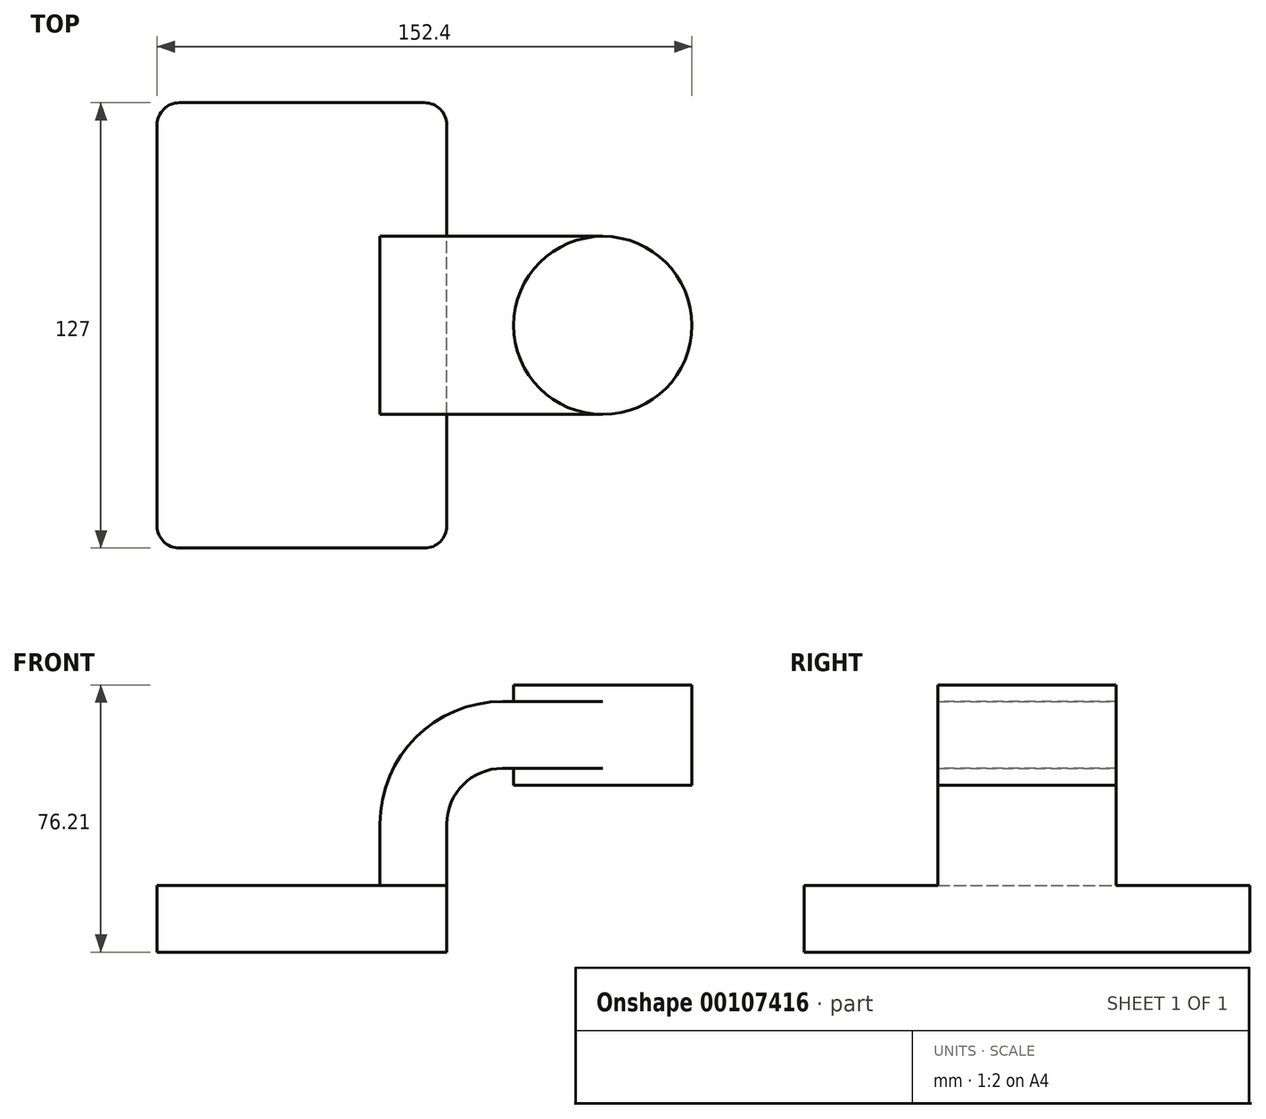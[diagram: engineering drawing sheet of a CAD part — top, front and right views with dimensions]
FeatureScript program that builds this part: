
annotation { "Feature Type Name" : "Feature", "Feature Type Description" : "" }
export const myFeature = defineFeature(function(context is Context, id is Id, definition is map)
    precondition{}
    {
        {
            var Q0;
            Q0=qCreatedBy(makeId("Front.planeOp"),FACE);
            var sketch = newSketch(context, id + "F0", { "sketchPlane" : qUnion([Q0])});
            skLineSegment(sketch, "E0.bottom", {"start": v(41.27, 9.53) * mm, "end": v(-41.28, 9.53) * mm});
            skLineSegment(sketch, "E0.top", {"start": v(41.28, -9.52) * mm, "end": v(-41.27, -9.52) * mm});
            skLineSegment(sketch, "E0.left", {"start": v(41.28, 9.53) * mm, "end": v(41.28, -9.52) * mm});
            skLineSegment(sketch, "E0.right", {"start": v(-41.28, 9.53) * mm, "end": v(-41.27, -9.52) * mm});
            skPoint(sketch, "E0.middle", {"position": v(0, 0) * mm});
            skLineSegment(sketch, "E1.bottom", {"start": v(60.33, 38.1) * mm, "end": v(111.13, 38.1) * mm});
            skLineSegment(sketch, "E1.top", {"start": v(60.33, 66.68) * mm, "end": v(111.13, 66.68) * mm});
            skLineSegment(sketch, "E1.left", {"start": v(60.33, 38.1) * mm, "end": v(60.33, 66.67) * mm});
            skLineSegment(sketch, "E1.right", {"start": v(111.13, 38.1) * mm, "end": v(111.13, 66.68) * mm});
            skPoint(sketch, "E1.middle", {"position": v(85.73, 52.39) * mm});
            skLineSegment(sketch, "E2", {"start": v(41.27, 9.53) * mm, "end": v(41.27, 27) * mm});
            skArc(sketch, "E3", {"start": v(41.27, 27) * mm, "mid": v(45.92, 38.23) * mm, "end": v(57.15, 42.88) * mm});
            skLineSegment(sketch, "E4", {"start": v(57.15, 42.88) * mm, "end": v(85.73, 42.88) * mm});
            skLineSegment(sketch, "E5.0", {"start": v(57.15, 61.93) * mm, "end": v(85.73, 61.93) * mm});
            skArc(sketch, "E5.1", {"start": v(22.23, 27) * mm, "mid": v(32.45, 51.7) * mm, "end": v(57.15, 61.93) * mm});
            skLineSegment(sketch, "E5.2", {"start": v(22.22, 9.53) * mm, "end": v(22.22, 27) * mm});
            skLineSegment(sketch, "E6", {"start": v(85.73, 66.68) * mm, "end": v(85.73, 38.1) * mm});
            skFitSpline(sketch, "E7", {"points": [v(-41.28, 9.52) * mm, v(57.15, 61.93) * mm], "startDerivative": vector(0.32, 75.35) * mm, "endDerivative": vector(119.06, -1.1) * mm});
            skSolve(sketch);
        }
        {
            var Q0;
            Q0=makeQuery(id+"F0.imprint","IMPRINT",FACE,{"disambiguationData":[TD([[makeQuery(id+"F0.imprint","IMPRINT",EDGE,{"derivedFrom":sQuery(id+"F0.wireOp",EDGE,"E0.top")}),-1.0]])]});
            extrude(context, id + "F1", {"entities" : qUnion([Q0]), "endBound" : BoundingType.SYMMETRIC, "depth" : 127 * mm});
        }
        {
            var Q0;
            {var subQ1=sQuery(id+"F0.wireOp",EDGE,"E2");Q0=makeQuery(id+"F0.imprint","IMPRINT",FACE,{"disambiguationData":[TD([[makeQuery(id+"F0.imprint","IMPRINT",EDGE,{"derivedFrom":subQ1}),1.0]])]});}
            extrude(context, id + "F2", {"entities" : qUnion([Q0]), "operationType" : NewBodyOperationType.ADD, "endBound" : BoundingType.SYMMETRIC, "depth" : 50.8 * mm});
        }
        {
            var Q0;
            Q0=makeQuery(id+"F0.imprint","IMPRINT",FACE,{"disambiguationData":[TD([[makeQuery(id+"F0.imprint","IMPRINT",EDGE,{"derivedFrom":sQuery(id+"F0.wireOp",EDGE,"E5.1")}),1.0]])]});
            extrude(context, id + "F3", {"entities" : qUnion([Q0]), "operationType" : NewBodyOperationType.ADD, "endBound" : BoundingType.SYMMETRIC, "depth" : 15.88 * mm});
        }
        {
            var Q0;
            {var subQ0=sQuery(id+"F0.wireOp",EDGE,"E4");var subQ1=sQuery(id+"F0.wireOp",EDGE,"E1.left");var subQ2=makeQuery(id+"F0.imprint","INTERSECT",VERTEX,{"derivedFrom":[subQ1,subQ0]});Q0=makeQuery(id+"F0.imprint","IMPRINT",FACE,{"disambiguationData":[TD([[makeQuery(id+"F0.imprint","IMPRINT",EDGE,{"disambiguationData":[TD([[subQ2,-1.0]])],"derivedFrom":subQ1}),-1.0]])]});}
            extrude(context, id + "F4", {"entities" : qUnion([Q0]), "operationType" : NewBodyOperationType.ADD, "endBound" : BoundingType.SYMMETRIC, "depth" : 50.8 * mm});
        }
        {
            var Q0;
            {var subQ0=sQuery(id+"F0.wireOp",EDGE,"E1.right");Q0=makeQuery(id+"F0.imprint","IMPRINT",FACE,{"disambiguationData":[TD([[makeQuery(id+"F0.imprint","IMPRINT",EDGE,{"derivedFrom":subQ0}),1.0]])]});}
            var Q1;
            Q1=sQuery(id+"F0.wireOp",EDGE,"E6");
            revolve(context, id + "F5", {"operationType" : NewBodyOperationType.ADD, "entities" : qUnion([Q0]), "axis" : qUnion([Q1]), "revolveType" : RevolveType.FULL});
        }
        {
            var Q0;
            Q0=makeQuery(id+"F1.opExtrude","CAP_EDGE",EDGE,{"disambiguationData":[OSD([sQuery(id+"F0.wireOp",EDGE,"E0.left")])],"isStart":false});
            var Q1;
            Q1=makeQuery(id+"F1.opExtrude","CAP_EDGE",EDGE,{"disambiguationData":[OSD([sQuery(id+"F0.wireOp",EDGE,"E0.right")])],"isStart":false});
            var Q2;
            Q2=makeQuery(id+"F1.opExtrude","CAP_EDGE",EDGE,{"disambiguationData":[OSD([sQuery(id+"F0.wireOp",EDGE,"E0.left")])],"isStart":true});
            var Q3;
            Q3=makeQuery(id+"F1.opExtrude","CAP_EDGE",EDGE,{"disambiguationData":[OSD([sQuery(id+"F0.wireOp",EDGE,"E0.right")])],"isStart":true});
            fillet(context, id + "F6", {"entities" : qUnion([Q0, Q1, Q2, Q3]), "radius" : 6.35 * mm, "tangentPropagation" : true, "allowEdgeOverflow" : false});
        }
    });
